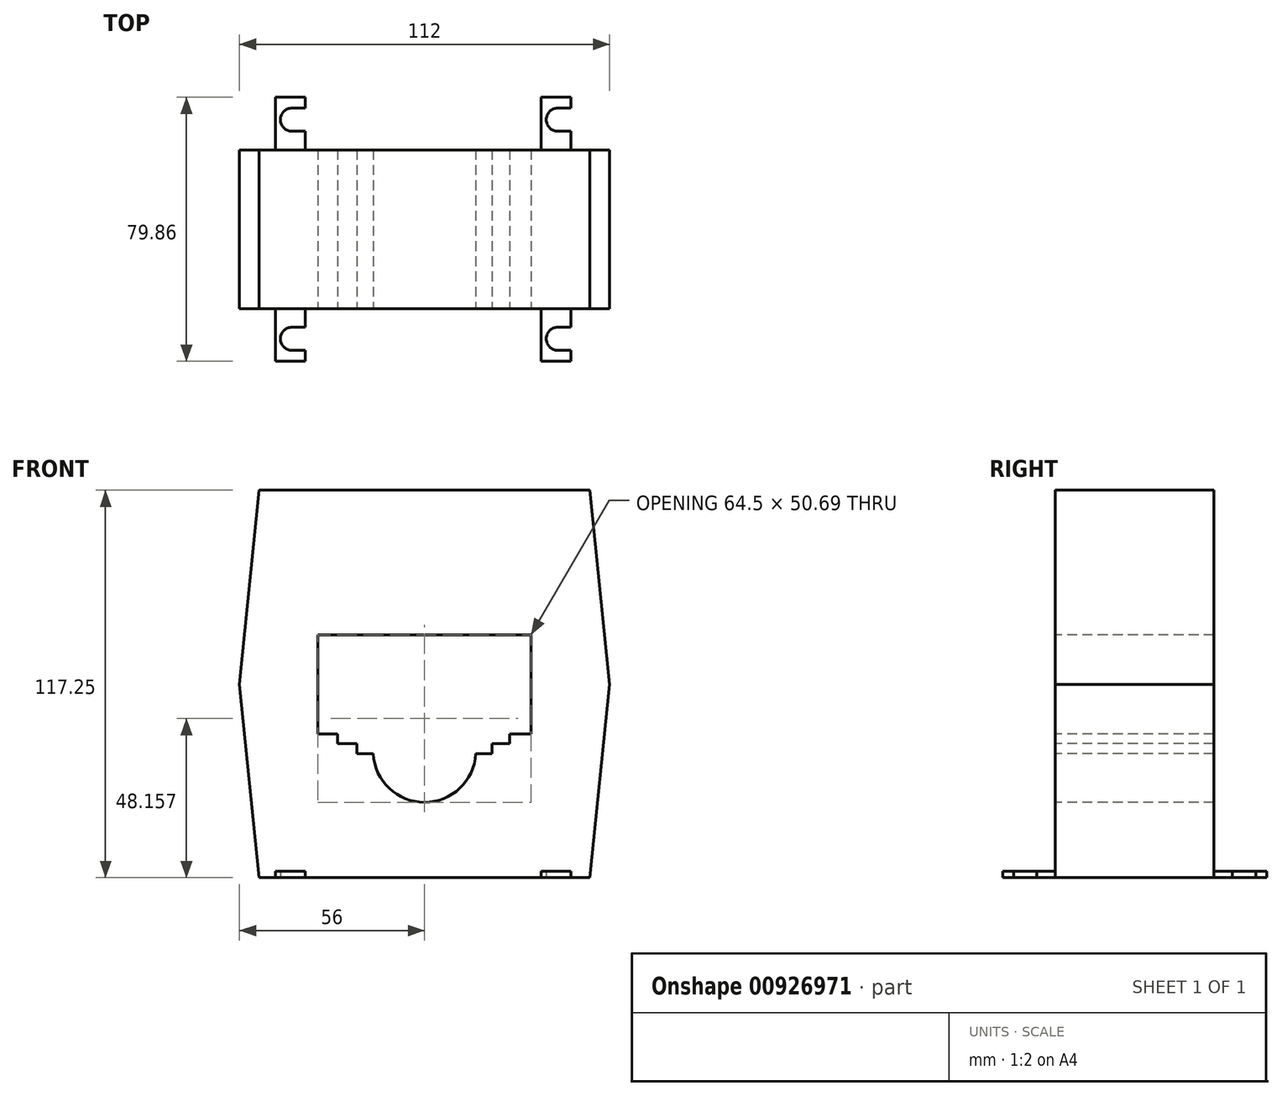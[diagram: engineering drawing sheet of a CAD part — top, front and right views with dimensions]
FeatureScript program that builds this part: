
annotation { "Feature Type Name" : "Feature", "Feature Type Description" : "" }
export const myFeature = defineFeature(function(context is Context, id is Id, definition is map)
    precondition{}
    {
        {
            var Q0;
            Q0=qCreatedBy(makeId("Front.planeOp"),FACE);
            var sketch = newSketch(context, id + "F0", { "sketchPlane" : qUnion([Q0])});
            skLineSegment(sketch, "E0", {"start": v(0, -58.5) * mm, "end": v(50, -58.5) * mm});
            skLineSegment(sketch, "E1", {"start": v(0, -58.5) * mm, "end": v(40, -58.5) * mm});
            skLineSegment(sketch, "E2", {"start": v(0, -58.5) * mm, "end": v(-40, -58.5) * mm});
            skLineSegment(sketch, "E3", {"start": v(-56, 0) * mm, "end": v(-50, -58.5) * mm});
            skLineSegment(sketch, "E4", {"start": v(56, 0) * mm, "end": v(50, -58.5) * mm});
            skLineSegment(sketch, "E5", {"start": v(0, 58.75) * mm, "end": v(-50, 58.75) * mm});
            skLineSegment(sketch, "E6", {"start": v(0, 58.75) * mm, "end": v(50, 58.75) * mm});
            skLineSegment(sketch, "E7", {"start": v(0, -58.5) * mm, "end": v(-50, -58.5) * mm});
            skLineSegment(sketch, "E8", {"start": v(50, 58.75) * mm, "end": v(56, 0) * mm});
            skLineSegment(sketch, "E9", {"start": v(-56, 0) * mm, "end": v(-50, 58.75) * mm});
            skLineSegment(sketch, "E10", {"start": v(0, 15) * mm, "end": v(32.25, 15) * mm});
            skLineSegment(sketch, "E11", {"start": v(32.25, 15) * mm, "end": v(32.25, -15) * mm});
            skLineSegment(sketch, "E12", {"start": v(32.25, -15) * mm, "end": v(25.75, -15) * mm});
            skLineSegment(sketch, "E13", {"start": v(25.75, -15) * mm, "end": v(25.75, -18) * mm});
            skLineSegment(sketch, "E14", {"start": v(25.75, -18) * mm, "end": v(20.5, -18) * mm});
            skLineSegment(sketch, "E15", {"start": v(0, 15) * mm, "end": v(-32.25, 15) * mm});
            skLineSegment(sketch, "E16", {"start": v(-32.25, 15) * mm, "end": v(-32.25, -15) * mm});
            skLineSegment(sketch, "E17", {"start": v(-32.25, -15) * mm, "end": v(-26.25, -15) * mm});
            skLineSegment(sketch, "E18", {"start": v(-26.25, -15) * mm, "end": v(-26.25, -18) * mm});
            skLineSegment(sketch, "E19", {"start": v(-26.25, -18) * mm, "end": v(-20.5, -18) * mm});
            skLineSegment(sketch, "E20", {"start": v(-20.5, -18) * mm, "end": v(-20.5, -21) * mm});
            skLineSegment(sketch, "E21", {"start": v(20.5, -21) * mm, "end": v(20.5, -18) * mm});
            skLineSegment(sketch, "E22", {"start": v(-20.5, -21) * mm, "end": v(-15.5, -21) * mm});
            skLineSegment(sketch, "E23", {"start": v(15.5, -21) * mm, "end": v(20.5, -21) * mm});
            skArc(sketch, "E24", {"start": v(-15.5, -21) * mm, "mid": v(0, -35.69) * mm, "end": v(15.5, -21) * mm});
            skSolve(sketch);
        }
        {
            var Q0;
            Q0=makeQuery(id+"F0.imprint","IMPRINT",FACE,{"disambiguationData":[TD([[makeQuery(id+"F0.imprint","IMPRINT",EDGE,{"derivedFrom":sQuery(id+"F0.wireOp",EDGE,"E0")}),1.0]])]});
            var Q1;
            Q1=sQuery(id+"F0.wireOp",EDGE,"E4");
            var Q2;
            Q2=sQuery(id+"F0.wireOp",EDGE,"JVzqgXMn-iqVn-cR1m-GP61-PTJAuJzW3dDI");
            var Q3;
            Q3=sQuery(id+"F0.wireOp",EDGE,"dXRZ8FcZ-7CHE-rDIB-6l9W-4eIOKC150MIz");
            var Q4;
            Q4=sQuery(id+"F0.wireOp",EDGE,"2x4D3XNR-Kyy8-Nqiz-MLaU-d1TwL1m5PH7z");
            var Q5;
            Q5=sQuery(id+"F0.wireOp",EDGE,"E3");
            var Q6;
            Q6=sQuery(id+"F0.wireOp",EDGE,"VewHAryc-UasI-veL3-6nRF-5sfaNTymT8WS");
            extrude(context, id + "F1", {"entities" : qUnion([Q0]), "surfaceEntities" : qUnion([Q1, Q2, Q3, Q4, Q5, Q6]), "endBound" : BoundingType.SYMMETRIC, "oppositeDirection" : true, "depth" : 48 * mm, "offsetDistance" : 25 * mm});
        }
        {
            var Q0;
            Q0=makeQuery(id+"F1.opExtrude","SWEPT_FACE",FACE,{"disambiguationData":[OSD([sQuery(id+"F0.wireOp",EDGE,"E0"),sQuery(id+"F0.wireOp",EDGE,"E1"),sQuery(id+"F0.wireOp",EDGE,"E7")])]});
            var sketch = newSketch(context, id + "F2", { "sketchPlane" : qUnion([Q0])});
            skLineSegment(sketch, "E25.MirrorCS", {"start": v(44.36, -39.93) * mm, "end": v(35.3, -39.93) * mm});
            skLineSegment(sketch, "E26.MirrorCS", {"start": v(40.36, -33.13) * mm, "end": v(40.36, -36.63) * mm});
            skLineSegment(sketch, "E27.MirrorCS", {"start": v(-40.1, -33.13) * mm, "end": v(-40.1, -29.63) * mm});
            skLineSegment(sketch, "E28.MirrorCS", {"start": v(-40.1, 33.13) * mm, "end": v(-40.1, 29.63) * mm});
            skLineSegment(sketch, "E29.MirrorCS", {"start": v(-40.1, -33.13) * mm, "end": v(-40.1, -36.63) * mm});
            skLineSegment(sketch, "E30.MirrorCS", {"start": v(-45.14, 39.93) * mm, "end": v(-36.1, 39.93) * mm});
            skLineSegment(sketch, "E31.MirrorCS", {"start": v(-40.1, 33.13) * mm, "end": v(-40.1, 36.63) * mm});
            skLineSegment(sketch, "E32.MirrorCS", {"start": v(-45.14, -39.93) * mm, "end": v(-36.1, -39.93) * mm});
            skLineSegment(sketch, "E33", {"start": v(40.36, -33.13) * mm, "end": v(40.36, -29.63) * mm});
            skLineSegment(sketch, "E34", {"start": v(35.3, -39.93) * mm, "end": v(35.3, -24) * mm});
            skLineSegment(sketch, "E35", {"start": v(44.36, -39.93) * mm, "end": v(44.36, -24) * mm});
            skLineSegment(sketch, "E36", {"start": v(-45.14, -39.93) * mm, "end": v(-45.14, -24) * mm});
            skLineSegment(sketch, "E37", {"start": v(-36.1, -39.93) * mm, "end": v(-36.1, -24) * mm});
            skLineSegment(sketch, "E38", {"start": v(-45.14, 39.93) * mm, "end": v(-45.14, 24) * mm});
            skLineSegment(sketch, "E39", {"start": v(-36.1, 39.93) * mm, "end": v(-36.1, 24) * mm});
            skCircle(sketch, "E40", {"center": v(-40.1, -33.13) * mm, "radius": 3.5 * mm});
            skCircle(sketch, "E41", {"center": v(40.36, -33.13) * mm, "radius": 3.5 * mm});
            skCircle(sketch, "E42", {"center": v(-40.1, 33.13) * mm, "radius": 3.5 * mm});
            skLineSegment(sketch, "E43", {"start": v(-40.1, -36.63) * mm, "end": v(-36.1, -36.63) * mm});
            skLineSegment(sketch, "E44", {"start": v(-40.1, -29.63) * mm, "end": v(-36.1, -29.63) * mm});
            skLineSegment(sketch, "E45", {"start": v(-40.1, 29.63) * mm, "end": v(-36.1, 29.63) * mm});
            skLineSegment(sketch, "E46", {"start": v(-40.1, 36.63) * mm, "end": v(-36.1, 36.63) * mm});
            skLineSegment(sketch, "E47", {"start": v(40.36, -36.63) * mm, "end": v(44.36, -36.63) * mm});
            skLineSegment(sketch, "E48", {"start": v(40.36, -29.63) * mm, "end": v(44.36, -29.63) * mm});
            skLineSegment(sketch, "E49.MirrorCS", {"start": v(40.36, 33.13) * mm, "end": v(40.36, 29.63) * mm});
            skLineSegment(sketch, "E50.MirrorCS", {"start": v(40.36, 33.13) * mm, "end": v(40.36, 36.63) * mm});
            skLineSegment(sketch, "E51.MirrorCS", {"start": v(40.36, 29.63) * mm, "end": v(44.36, 29.63) * mm});
            skLineSegment(sketch, "E52.MirrorCS", {"start": v(44.36, 39.93) * mm, "end": v(44.36, 24) * mm});
            skLineSegment(sketch, "E53.MirrorCS", {"start": v(40.36, 36.63) * mm, "end": v(44.36, 36.63) * mm});
            skCircle(sketch, "E54.MirrorC", {"center": v(40.36, 33.13) * mm, "radius": 3.5 * mm});
            skLineSegment(sketch, "E55.MirrorCS", {"start": v(35.3, 39.93) * mm, "end": v(35.3, 24) * mm});
            skLineSegment(sketch, "E56.MirrorCS", {"start": v(44.36, 39.93) * mm, "end": v(35.3, 39.93) * mm});
            skSolve(sketch);
        }
        {
            var Q0;
            Q0=makeQuery(id+"F2.imprint","IMPRINT",FACE,{"disambiguationData":[TD([[makeQuery(id+"F2.imprint","IMPRINT",EDGE,{"derivedFrom":sQuery(id+"F2.wireOp",EDGE,"b83215a2-3eeb-40e1-8e2b-c616c080e92c")}),1.0]])]});
            var Q1;
            Q1=makeQuery(id+"F2.imprint","IMPRINT",FACE,{"disambiguationData":[TD([[makeQuery(id+"F2.imprint","IMPRINT",EDGE,{"derivedFrom":sQuery(id+"F2.wireOp",EDGE,"E30.MirrorCS")}),-1.0]])]});
            var Q2;
            Q2=makeQuery(id+"F2.imprint","IMPRINT",FACE,{"disambiguationData":[TD([[makeQuery(id+"F2.imprint","IMPRINT",EDGE,{"derivedFrom":sQuery(id+"F2.wireOp",EDGE,"E25.MirrorCS")}),-1.0]])]});
            var Q3;
            Q3=makeQuery(id+"F2.imprint","IMPRINT",FACE,{"disambiguationData":[TD([[makeQuery(id+"F2.imprint","IMPRINT",EDGE,{"derivedFrom":sQuery(id+"F2.wireOp",EDGE,"E32.MirrorCS")}),1.0]])]});
            var Q4;
            {var subQ5=sQuery(id+"F2.wireOp",EDGE,"E51.MirrorCS");Q4=makeQuery(id+"F2.imprint","IMPRINT",FACE,{"disambiguationData":[TD([[makeQuery(id+"F2.imprint","IMPRINT",EDGE,{"derivedFrom":subQ5}),-1.0]])]});}
            extrude(context, id + "F3", {"entities" : qUnion([Q0, Q1, Q2, Q3, Q4]), "oppositeDirection" : true, "depth" : 2 * mm, "offsetDistance" : 25 * mm});
        }
        {
            var Q0;
            {var subQ0=sQuery(id+"F0.wireOp",EDGE,"E15");Q0=makeQuery(id+"F0.imprint","IMPRINT",FACE,{"disambiguationData":[TD([[makeQuery(id+"F0.imprint","IMPRINT",EDGE,{"derivedFrom":subQ0}),1.0]])]});}
            var Q1;
            {var subQ0=sQuery(id+"F0.wireOp",EDGE,"E10");Q1=makeQuery(id+"F0.imprint","IMPRINT",FACE,{"disambiguationData":[TD([[makeQuery(id+"F0.imprint","IMPRINT",EDGE,{"derivedFrom":subQ0}),-1.0]])]});}
            extrude(context, id + "F4", {"entities" : qUnion([Q0, Q1]), "operationType" : NewBodyOperationType.REMOVE, "endBound" : BoundingType.SYMMETRIC, "oppositeDirection" : true, "depth" : 48 * mm, "offsetDistance" : 25 * mm});
        }
        {
            var Q0;
            {var subQ0=sQuery(id+"F2.wireOp",EDGE,"E27.MirrorCS");Q0=makeQuery(id+"F2.imprint","IMPRINT",FACE,{"disambiguationData":[TD([[makeQuery(id+"F2.imprint","IMPRINT",EDGE,{"derivedFrom":subQ0}),1.0]])]});}
            var Q1;
            {var subQ0=sQuery(id+"F2.wireOp",EDGE,"E27.MirrorCS");Q1=makeQuery(id+"F2.imprint","IMPRINT",FACE,{"disambiguationData":[TD([[makeQuery(id+"F2.imprint","IMPRINT",EDGE,{"derivedFrom":subQ0}),-1.0]])]});}
            var Q2;
            {var subQ0=sQuery(id+"F2.wireOp",EDGE,"E43");Q2=makeQuery(id+"F2.imprint","IMPRINT",FACE,{"disambiguationData":[TD([[makeQuery(id+"F2.imprint","IMPRINT",EDGE,{"derivedFrom":subQ0}),1.0]])]});}
            var Q3;
            {var subQ0=sQuery(id+"F2.wireOp",EDGE,"E28.MirrorCS");Q3=makeQuery(id+"F2.imprint","IMPRINT",FACE,{"disambiguationData":[TD([[makeQuery(id+"F2.imprint","IMPRINT",EDGE,{"derivedFrom":subQ0}),-1.0]])]});}
            var Q4;
            {var subQ0=sQuery(id+"F2.wireOp",EDGE,"E28.MirrorCS");Q4=makeQuery(id+"F2.imprint","IMPRINT",FACE,{"disambiguationData":[TD([[makeQuery(id+"F2.imprint","IMPRINT",EDGE,{"derivedFrom":subQ0}),1.0]])]});}
            var Q5;
            {var subQ0=sQuery(id+"F2.wireOp",EDGE,"E45");Q5=makeQuery(id+"F2.imprint","IMPRINT",FACE,{"disambiguationData":[TD([[makeQuery(id+"F2.imprint","IMPRINT",EDGE,{"derivedFrom":subQ0}),1.0]])]});}
            var Q6;
            {var subQ0=sQuery(id+"F2.wireOp",EDGE,"766bacd1-3607-494d-a4cb-03775a15285c");Q6=makeQuery(id+"F2.imprint","IMPRINT",FACE,{"disambiguationData":[TD([[makeQuery(id+"F2.imprint","IMPRINT",EDGE,{"derivedFrom":subQ0}),1.0]])]});}
            var Q7;
            {var subQ0=sQuery(id+"F2.wireOp",EDGE,"766bacd1-3607-494d-a4cb-03775a15285c");Q7=makeQuery(id+"F2.imprint","IMPRINT",FACE,{"disambiguationData":[TD([[makeQuery(id+"F2.imprint","IMPRINT",EDGE,{"derivedFrom":subQ0}),-1.0]])]});}
            var Q8;
            {var subQ0=sQuery(id+"F2.wireOp",EDGE,"9MRpXD2S-kTwM-KUVO-acGe-p8s2PdXSHVnq");Q8=makeQuery(id+"F2.imprint","IMPRINT",FACE,{"disambiguationData":[TD([[makeQuery(id+"F2.imprint","IMPRINT",EDGE,{"derivedFrom":subQ0}),1.0]])]});}
            var Q9;
            {var subQ0=sQuery(id+"F2.wireOp",EDGE,"E47");Q9=makeQuery(id+"F2.imprint","IMPRINT",FACE,{"disambiguationData":[TD([[makeQuery(id+"F2.imprint","IMPRINT",EDGE,{"derivedFrom":subQ0}),1.0]])]});}
            var Q10;
            {var subQ0=sQuery(id+"F2.wireOp",EDGE,"E26.MirrorCS");Q10=makeQuery(id+"F2.imprint","IMPRINT",FACE,{"disambiguationData":[TD([[makeQuery(id+"F2.imprint","IMPRINT",EDGE,{"derivedFrom":subQ0}),1.0]])]});}
            var Q11;
            {var subQ0=sQuery(id+"F2.wireOp",EDGE,"E26.MirrorCS");Q11=makeQuery(id+"F2.imprint","IMPRINT",FACE,{"disambiguationData":[TD([[makeQuery(id+"F2.imprint","IMPRINT",EDGE,{"derivedFrom":subQ0}),-1.0]])]});}
            var Q12;
            {var subQ0=sQuery(id+"F2.wireOp",EDGE,"E49.MirrorCS");Q12=makeQuery(id+"F2.imprint","IMPRINT",FACE,{"disambiguationData":[TD([[makeQuery(id+"F2.imprint","IMPRINT",EDGE,{"derivedFrom":subQ0}),-1.0]])]});}
            var Q13;
            {var subQ0=sQuery(id+"F2.wireOp",EDGE,"E49.MirrorCS");Q13=makeQuery(id+"F2.imprint","IMPRINT",FACE,{"disambiguationData":[TD([[makeQuery(id+"F2.imprint","IMPRINT",EDGE,{"derivedFrom":subQ0}),1.0]])]});}
            var Q14;
            {var subQ0=sQuery(id+"F2.wireOp",EDGE,"E51.MirrorCS");Q14=makeQuery(id+"F2.imprint","IMPRINT",FACE,{"disambiguationData":[TD([[makeQuery(id+"F2.imprint","IMPRINT",EDGE,{"derivedFrom":subQ0}),1.0]])]});}
            extrude(context, id + "F5", {"entities" : qUnion([Q0, Q1, Q2, Q3, Q4, Q5, Q6, Q7, Q8, Q9, Q10, Q11, Q12, Q13, Q14]), "operationType" : NewBodyOperationType.REMOVE, "oppositeDirection" : true, "depth" : 5 * mm, "offsetDistance" : 25 * mm});
        }
    });
